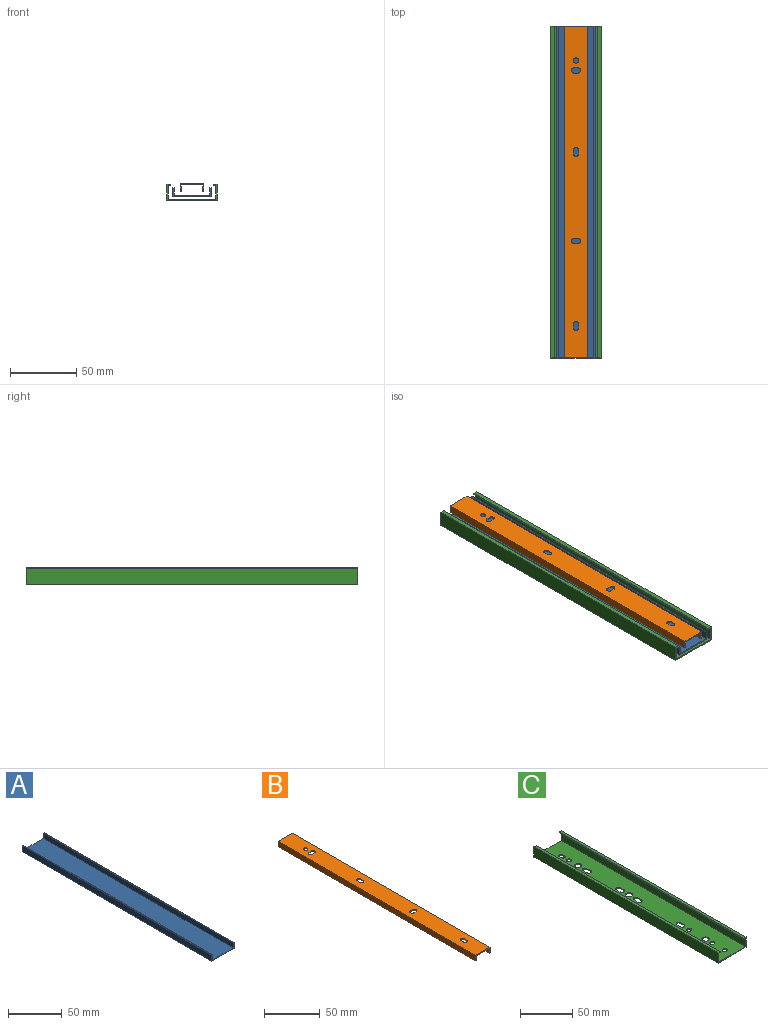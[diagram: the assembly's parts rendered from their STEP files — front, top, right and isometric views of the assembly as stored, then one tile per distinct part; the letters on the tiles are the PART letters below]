
ASSEMBLY  parts=3 mates=2
PART A: 10 faces, bbox 29x250x6.9 mm
  f0: plane 29x6.85mm, normal (0,1,0), area 40.7mm2, adj f1,f3,f4,f5,f6,f7,f8,f9
  f1: plane 250x1mm, normal (0,0,1), area 250mm2, adj f0,f2,f4,f6
  f2: plane 29x6.85mm, normal (0,-1,0), area 40.7mm2, adj f1,f3,f4,f5,f6,f7,f8,f9
  f3: plane 250x29mm, normal (0,0,-1), area 7250mm2, adj f0,f2,f4,f8
  f4: plane 250x6.85mm, normal (1,0,0), area 1712.5mm2, adj f0,f1,f2,f3
  f5: plane 250x27mm, normal (0,0,1), area 6750mm2, adj f0,f2,f6,f9
  f6: plane 250x5.85mm, normal (-1,0,0), area 1462.5mm2, adj f0,f1,f2,f5
  f7: plane 250x1mm, normal (0,0,1), area 250mm2, adj f0,f2,f8,f9
  f8: plane 250x6.85mm, normal (-1,0,0), area 1712.5mm2, adj f0,f2,f3,f7
  f9: plane 250x5.85mm, normal (1,0,0), area 1462.5mm2, adj f0,f2,f5,f7
PART B: 27 faces, bbox 18x250x6 mm
  f0: plane 250x16mm, normal (0,0,-1), area 3889.2mm2, adj f2,f4,f5,f7,f8,f9,f10,f11
  f1: plane 250x18mm, normal (0,0,1), area 4389.2mm2, adj f2,f4,f6,f7,f8,f9,f10,f11
  f2: plane 18x6mm, normal (0,1,0), area 28mm2, adj f0,f1,f3,f5,f6,f20,f21,f22
  f3: plane 250x1mm, normal (0,0,-1), area 250mm2, adj f2,f4,f5,f6
  f4: plane 18x6mm, normal (0,-1,0), area 28mm2, adj f0,f1,f3,f5,f6,f20,f21,f22
  f5: plane 250x5mm, normal (-1,0,0), area 1250mm2, adj f0,f2,f3,f4
  f6: plane 250x6mm, normal (1,0,0), area 1500mm2, adj f1,f2,f3,f4
  f7: plane 3x1mm, normal (0,1,0), area 3mm2, adj f0,f1,f8,f23
  f8: cylinder r=2mm len=4mm, axis (0,0,1), area 6.3mm2, adj f0,f1,f7,f9
  f9: plane 3x1mm, normal (0,-1,0), area 3mm2, adj f0,f1,f8,f23
  f10: cylinder r=2mm len=4mm, axis (0,0,1), area 6.3mm2, adj f0,f1,f11,f24
  f11: plane 3x1mm, normal (-1,0,0), area 3mm2, adj f0,f1,f10,f12
  f12: cylinder r=2mm len=4mm, axis (0,0,1), area 6.3mm2, adj f0,f1,f11,f24
  f13: cylinder r=2mm len=4mm, axis (0,0,1), area 6.3mm2, adj f0,f1,f15,f25
  f14: cylinder r=2mm len=4mm, axis (0,0,1), area 6.3mm2, adj f0,f1,f15,f25
  f15: plane 3x1mm, normal (-1,0,0), area 3mm2, adj f0,f1,f13,f14
  f16: plane 3x1mm, normal (0,-1,0), area 3mm2, adj f0,f1,f18,f26
  f17: plane 3x1mm, normal (0,1,0), area 3mm2, adj f0,f1,f18,f26
  f18: cylinder r=2mm len=4mm, axis (0,0,1), area 6.3mm2, adj f0,f1,f16,f17
  f19: cylinder r=2mm len=4mm, axis (0,0,1), area 12.6mm2, adj f0,f1
  f20: plane 250x1mm, normal (0,0,-1), area 250mm2, adj f2,f4,f21,f22
  f21: plane 250x5mm, normal (1,0,0), area 1250mm2, adj f0,f2,f4,f20
  f22: plane 250x6mm, normal (-1,0,0), area 1500mm2, adj f1,f2,f4,f20
  f23: cylinder r=2mm len=4mm, axis (0,0,1), area 6.3mm2, adj f0,f1,f7,f9
  f24: plane 3x1mm, normal (1,0,0), area 3mm2, adj f0,f1,f10,f12
  f25: plane 3x1mm, normal (1,0,0), area 3mm2, adj f0,f1,f13,f14
  f26: cylinder r=2mm len=4mm, axis (0,0,1), area 6.3mm2, adj f0,f1,f16,f17
PART C: 41 faces, bbox 38x250x12 mm
  f0: plane 250x38mm, normal (0,0,-1), area 9102.9mm2, adj f2,f4,f5,f9,f10,f11,f12,f13
  f1: plane 250x36mm, normal (0,0,1), area 8602.9mm2, adj f2,f4,f7,f9,f10,f11,f12,f13
  f2: plane 38x12mm, normal (0,1,0), area 64mm2, adj f0,f1,f3,f5,f6,f7,f8,f31
  f3: plane 250x1mm, normal (-1,0,0), area 250mm2, adj f2,f4,f6,f8
  f4: plane 38x12mm, normal (0,-1,0), area 64mm2, adj f0,f1,f3,f5,f6,f7,f8,f31
  f5: plane 250x12mm, normal (1,0,0), area 3000mm2, adj f0,f2,f4,f6
  f6: plane 250x3mm, normal (0,0,1), area 750mm2, adj f2,f3,f4,f5
  f7: plane 250x10mm, normal (-1,0,0), area 2500mm2, adj f1,f2,f4,f8
  f8: plane 250x2mm, normal (0,0,-1), area 500mm2, adj f2,f3,f4,f7
  f9: cylinder r=2.5mm len=5mm, axis (0,0,-1), area 15.7mm2, adj f0,f1
  f10: cylinder r=3.5mm len=7mm, axis (0,0,-1), area 22mm2, adj f0,f1
  f11: cylinder r=2.5mm len=5mm, axis (0,0,-1), area 15.7mm2, adj f0,f1
  f12: cylinder r=3.5mm len=7mm, axis (0,0,-1), area 22mm2, adj f0,f1
  f13: plane 5x1mm, normal (-1,0,0), area 5mm2, adj f0,f1,f14,f15
  f14: cylinder r=2.5mm len=5mm, axis (0,0,-1), area 7.9mm2, adj f0,f1,f13,f36
  f15: cylinder r=2.5mm len=5mm, axis (0,0,-1), area 7.9mm2, adj f0,f1,f13,f36
  f16: plane 3x1mm, normal (-1,0,0), area 3mm2, adj f0,f1,f17,f18
  f17: cylinder r=2mm len=4mm, axis (0,0,-1), area 6.3mm2, adj f0,f1,f16,f37
  f18: cylinder r=2mm len=4mm, axis (0,0,-1), area 6.3mm2, adj f0,f1,f16,f37
  f19: cylinder r=2.5mm len=5mm, axis (0,0,-1), area 15.7mm2, adj f0,f1
  f20: cylinder r=3.5mm len=7mm, axis (0,0,-1), area 22mm2, adj f0,f1
  f21: plane 5x1mm, normal (-1,0,0), area 5mm2, adj f0,f1,f22,f23
  f22: cylinder r=2.5mm len=5mm, axis (0,0,-1), area 7.9mm2, adj f0,f1,f21,f38
  f23: cylinder r=2.5mm len=5mm, axis (0,0,-1), area 7.9mm2, adj f0,f1,f21,f38
  f24: plane 5x1mm, normal (-1,0,0), area 5mm2, adj f0,f1,f25,f26
  f25: cylinder r=2.5mm len=5mm, axis (0,0,-1), area 7.9mm2, adj f0,f1,f24,f39
  f26: cylinder r=2.5mm len=5mm, axis (0,0,-1), area 7.9mm2, adj f0,f1,f24,f39
  f27: plane 5x1mm, normal (-1,0,0), area 5mm2, adj f0,f1,f28,f29
  f28: cylinder r=2.5mm len=5mm, axis (0,0,-1), area 7.9mm2, adj f0,f1,f27,f40
  f29: cylinder r=2.5mm len=5mm, axis (0,0,-1), area 7.9mm2, adj f0,f1,f27,f40
  f30: cylinder r=2.5mm len=5mm, axis (0,0,-1), area 15.7mm2, adj f0,f1
  f31: plane 250x1mm, normal (1,0,0), area 250mm2, adj f2,f4,f33,f35
  f32: plane 250x12mm, normal (-1,0,0), area 3000mm2, adj f0,f2,f4,f33
  f33: plane 250x3mm, normal (0,0,1), area 750mm2, adj f2,f4,f31,f32
  f34: plane 250x10mm, normal (1,0,0), area 2500mm2, adj f1,f2,f4,f35
  f35: plane 250x2mm, normal (0,0,-1), area 500mm2, adj f2,f4,f31,f34
  f36: plane 5x1mm, normal (1,0,0), area 5mm2, adj f0,f1,f14,f15
  f37: plane 3x1mm, normal (1,0,0), area 3mm2, adj f0,f1,f17,f18
  f38: plane 5x1mm, normal (1,0,0), area 5mm2, adj f0,f1,f22,f23
  f39: plane 5x1mm, normal (1,0,0), area 5mm2, adj f0,f1,f25,f26
  f40: plane 5x1mm, normal (1,0,0), area 5mm2, adj f0,f1,f28,f29
PLACE A at identity
PLACE B at identity
PLACE C at identity fixed
MATE slider C.f2 <-> A.f0  axis (0,-1,0) through (0,0,0)mm
MATE slider A.f0 <-> B.f2  axis (0,-1,0) through (0,0,0)mm
